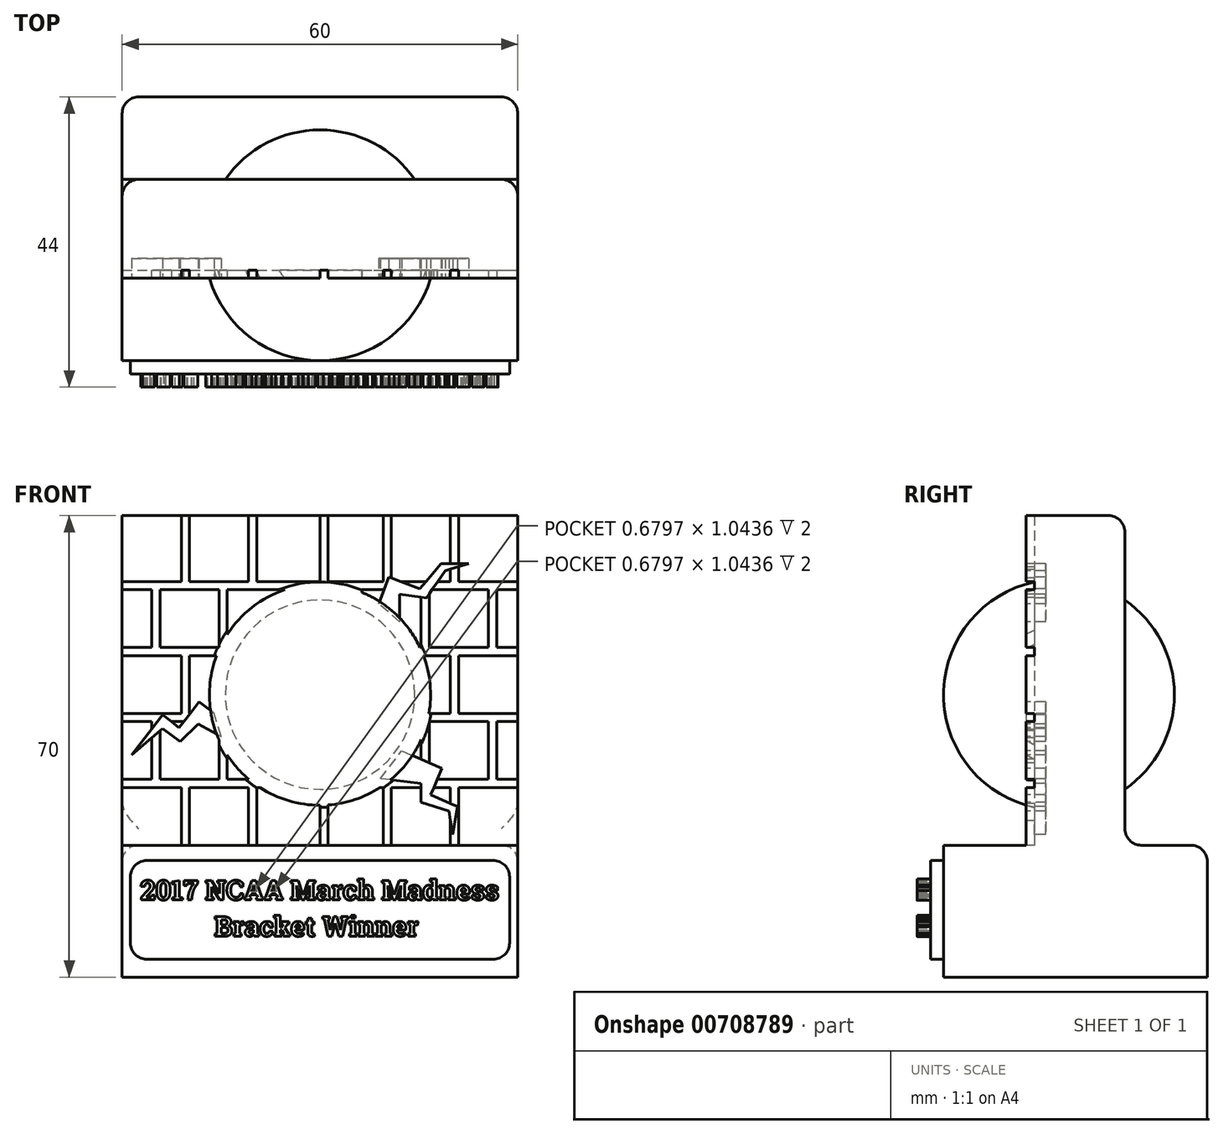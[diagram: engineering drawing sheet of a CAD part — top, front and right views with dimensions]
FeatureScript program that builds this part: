
annotation { "Feature Type Name" : "Feature", "Feature Type Description" : "" }
export const myFeature = defineFeature(function(context is Context, id is Id, definition is map)
    precondition{}
    {
        {
            var Q0;
            Q0=qCreatedBy(makeId("Top.planeOp"),FACE);
            var sketch = newSketch(context, id + "F0", { "sketchPlane" : qUnion([Q0])});
            skLineSegment(sketch, "E0.bottom", {"start": v(30, -20) * mm, "end": v(-30, -20) * mm});
            skLineSegment(sketch, "E0.top", {"start": v(30, 20) * mm, "end": v(-30, 20) * mm});
            skLineSegment(sketch, "E0.left", {"start": v(30, -20) * mm, "end": v(30, 20) * mm});
            skLineSegment(sketch, "E0.right", {"start": v(-30, -20) * mm, "end": v(-30, 20) * mm});
            skPoint(sketch, "E0.middle", {"position": v(0, 0) * mm});
            skSolve(sketch);
        }
        {
            var Q0;
            Q0=makeQuery(id+"F0.imprint","IMPRINT",FACE,{"disambiguationData":[TD([[makeQuery(id+"F0.imprint","IMPRINT",EDGE,{"derivedFrom":sQuery(id+"F0.wireOp",EDGE,"E0.bottom")}),-1.0]])]});
            extrude(context, id + "F1", {"entities" : qUnion([Q0]), "depth" : 20 * mm, "offsetDistance" : 25 * mm});
        }
        {
            var Q0;
            Q0=makeQuery(id+"F1.opExtrude","CAP_FACE",FACE,{"disambiguationData":[OSD([sQuery(id+"F0.wireOp",EDGE,"E0.bottom"),sQuery(id+"F0.wireOp",EDGE,"E0.top"),sQuery(id+"F0.wireOp",EDGE,"E0.left"),sQuery(id+"F0.wireOp",EDGE,"E0.right")])],"isStart":false});
            var sketch = newSketch(context, id + "F2", { "sketchPlane" : qUnion([Q0])});
            skLineSegment(sketch, "E1.bottom", {"start": v(30, -7.5) * mm, "end": v(-30, -7.5) * mm});
            skLineSegment(sketch, "E1.top", {"start": v(30, 7.5) * mm, "end": v(-30, 7.5) * mm});
            skLineSegment(sketch, "E1.left", {"start": v(30, -7.5) * mm, "end": v(30, 7.5) * mm});
            skLineSegment(sketch, "E1.right", {"start": v(-30, -7.5) * mm, "end": v(-30, 7.5) * mm});
            skPoint(sketch, "E1.middle", {"position": v(0, 0) * mm});
            skSolve(sketch);
        }
        {
            var Q0;
            Q0 = qSketchRegion(id + "F2", true);
            extrude(context, id + "F3", {"entities" : qUnion([Q0]), "operationType" : NewBodyOperationType.ADD, "depth" : 50 * mm, "offsetDistance" : 25 * mm});
        }
        {
            var Q0;
            Q0=makeQuery(id+"F3.opExtrude","SWEPT_FACE",FACE,{"disambiguationData":[OSD([sQuery(id+"F2.wireOp",EDGE,"E1.bottom")])]});
            var sketch = newSketch(context, id + "F4", { "sketchPlane" : qUnion([Q0])});
            skSolve(sketch);
        }
        {
            var Q0;
            {var subQ0=sQuery(id+"F2.wireOp",EDGE,"E1.bottom");Q0=makeQuery(id+"F4.imprint","IMPRINT",FACE,{"disambiguationData":[TD([[makeQuery(id+"F4.imprint","IMPRINT",EDGE,{"derivedFrom":makeQuery(id+"F3.opExtrude","CAP_EDGE",EDGE,{"disambiguationData":[OSD([subQ0])],"isStart":false})}),1.0]])]});}
            var sketch = newSketch(context, id + "F5", { "sketchPlane" : qUnion([Q0])});
            skLineSegment(sketch, "E2", {"start": v(-30, 60) * mm, "end": v(-21.04, 60) * mm});
            skLineSegment(sketch, "E3", {"start": v(-30, 50) * mm, "end": v(-25.52, 50) * mm});
            skLineSegment(sketch, "E4", {"start": v(-30, 40) * mm, "end": v(-21.04, 40) * mm});
            skLineSegment(sketch, "E5", {"start": v(-30, 30) * mm, "end": v(-25.52, 30) * mm});
            skLineSegment(sketch, "E6", {"start": v(-30, 58.75) * mm, "end": v(-25.52, 58.75) * mm});
            skLineSegment(sketch, "E7", {"start": v(-30, 48.75) * mm, "end": v(-21.04, 48.75) * mm});
            skLineSegment(sketch, "E8", {"start": v(-30, 38.75) * mm, "end": v(-25.52, 38.75) * mm});
            skLineSegment(sketch, "E9", {"start": v(-30, 28.75) * mm, "end": v(-21.04, 28.75) * mm});
            skLineSegment(sketch, "E10", {"start": v(-30, 60) * mm, "end": v(-30, 58.75) * mm});
            skLineSegment(sketch, "E11", {"start": v(30, 60) * mm, "end": v(30, 58.75) * mm});
            skLineSegment(sketch, "E12.bottom", {"start": v(-21.04, 70) * mm, "end": v(-19.79, 70) * mm});
            skLineSegment(sketch, "E12.left", {"start": v(-21.04, 70) * mm, "end": v(-21.04, 60) * mm});
            skLineSegment(sketch, "E12.right", {"start": v(-19.79, 70) * mm, "end": v(-19.79, 60) * mm});
            skLineSegment(sketch, "E13.bottom", {"start": v(-10.83, 70) * mm, "end": v(-9.58, 70) * mm});
            skLineSegment(sketch, "E13.left", {"start": v(-10.83, 70) * mm, "end": v(-10.83, 60) * mm});
            skLineSegment(sketch, "E13.right", {"start": v(-9.58, 70) * mm, "end": v(-9.58, 60) * mm});
            skLineSegment(sketch, "E14.bottom", {"start": v(9.58, 70) * mm, "end": v(10.83, 70) * mm});
            skLineSegment(sketch, "E14.left", {"start": v(9.58, 70) * mm, "end": v(9.58, 60) * mm});
            skLineSegment(sketch, "E14.right", {"start": v(10.83, 70) * mm, "end": v(10.83, 60) * mm});
            skLineSegment(sketch, "E15.bottom", {"start": v(19.79, 70) * mm, "end": v(21.04, 70) * mm});
            skLineSegment(sketch, "E15.left", {"start": v(19.79, 70) * mm, "end": v(19.79, 60) * mm});
            skLineSegment(sketch, "E15.right", {"start": v(21.04, 70) * mm, "end": v(21.04, 60) * mm});
            skLineSegment(sketch, "E16.top", {"start": v(1.24, 70) * mm, "end": v(-0.01, 70) * mm});
            skLineSegment(sketch, "E16.left", {"start": v(1.24, 60) * mm, "end": v(1.24, 70) * mm});
            skLineSegment(sketch, "E16.right", {"start": v(-0.01, 60) * mm, "end": v(-0.01, 70) * mm});
            skPoint(sketch, "E16.middle", {"position": v(0.61, 65) * mm});
            skLineSegment(sketch, "E17.0", {"start": v(-21.04, 20) * mm, "end": v(-19.79, 20) * mm});
            skLineSegment(sketch, "E18.trimOffspring", {"start": v(-21.04, 48.75) * mm, "end": v(-21.04, 40) * mm});
            skLineSegment(sketch, "E19.trimOffspring", {"start": v(-19.79, 48.75) * mm, "end": v(-19.79, 40) * mm});
            skLineSegment(sketch, "E20.trimOffspring", {"start": v(-10.83, 48.75) * mm, "end": v(-10.83, 40) * mm});
            skLineSegment(sketch, "E21.trimOffspring", {"start": v(-9.58, 48.75) * mm, "end": v(-9.58, 40) * mm});
            skLineSegment(sketch, "E22.trimOffspring", {"start": v(-0.01, 48.75) * mm, "end": v(-0.01, 40) * mm});
            skLineSegment(sketch, "E23.trimOffspring", {"start": v(1.24, 48.75) * mm, "end": v(1.24, 40) * mm});
            skLineSegment(sketch, "E24.trimOffspring", {"start": v(9.58, 48.75) * mm, "end": v(9.58, 40) * mm});
            skLineSegment(sketch, "E25.trimOffspring", {"start": v(10.83, 48.75) * mm, "end": v(10.83, 40) * mm});
            skLineSegment(sketch, "E26.trimOffspring", {"start": v(19.79, 48.75) * mm, "end": v(19.79, 40) * mm});
            skLineSegment(sketch, "E27.trimOffspring", {"start": v(21.04, 48.75) * mm, "end": v(21.04, 40) * mm});
            skLineSegment(sketch, "E28.trimOffspring", {"start": v(-21.04, 28.75) * mm, "end": v(-21.04, 20) * mm});
            skLineSegment(sketch, "E29.trimOffspring", {"start": v(-19.79, 28.75) * mm, "end": v(-19.79, 20) * mm});
            skLineSegment(sketch, "E30.trimOffspring", {"start": v(-10.83, 28.75) * mm, "end": v(-10.83, 20) * mm});
            skLineSegment(sketch, "E31.trimOffspring", {"start": v(-9.58, 28.75) * mm, "end": v(-9.58, 20) * mm});
            skLineSegment(sketch, "E32.trimOffspring", {"start": v(-0.01, 28.75) * mm, "end": v(-0.01, 20) * mm});
            skLineSegment(sketch, "E33.trimOffspring", {"start": v(9.58, 28.75) * mm, "end": v(9.58, 20) * mm});
            skLineSegment(sketch, "E34.trimOffspring", {"start": v(10.83, 28.75) * mm, "end": v(10.83, 20) * mm});
            skLineSegment(sketch, "E35.trimOffspring", {"start": v(19.79, 28.75) * mm, "end": v(19.79, 20) * mm});
            skLineSegment(sketch, "E36.trimOffspring", {"start": v(21.04, 28.75) * mm, "end": v(21.04, 20) * mm});
            skLineSegment(sketch, "E37.trimOffspring", {"start": v(-9.58, 60) * mm, "end": v(9.58, 60) * mm});
            skLineSegment(sketch, "E38.trimOffspring", {"start": v(-19.79, 60) * mm, "end": v(-10.83, 60) * mm});
            skLineSegment(sketch, "E39.trimOffspring", {"start": v(10.83, 48.75) * mm, "end": v(19.79, 48.75) * mm});
            skPoint(sketch, "E40.firstSnap0", {"position": v(-25.52, 60) * mm});
            skLineSegment(sketch, "E40.left", {"start": v(-25.52, 58.75) * mm, "end": v(-25.52, 50) * mm});
            skLineSegment(sketch, "E40.right", {"start": v(-24.27, 58.75) * mm, "end": v(-24.27, 50) * mm});
            skLineSegment(sketch, "E41.left", {"start": v(-15.3, 58.75) * mm, "end": v(-15.3, 50) * mm});
            skLineSegment(sketch, "E41.right", {"start": v(-14.06, 58.75) * mm, "end": v(-14.06, 50) * mm});
            skLineSegment(sketch, "E42.left", {"start": v(-5.1, 58.75) * mm, "end": v(-5.1, 50) * mm});
            skLineSegment(sketch, "E42.right", {"start": v(-3.85, 58.75) * mm, "end": v(-3.85, 50) * mm});
            skLineSegment(sketch, "E43.left", {"start": v(5.11, 58.75) * mm, "end": v(5.11, 50) * mm});
            skLineSegment(sketch, "E43.right", {"start": v(6.36, 58.75) * mm, "end": v(6.36, 50) * mm});
            skLineSegment(sketch, "E44.left", {"start": v(15.32, 58.75) * mm, "end": v(15.32, 50) * mm});
            skLineSegment(sketch, "E44.right", {"start": v(16.57, 58.75) * mm, "end": v(16.57, 50) * mm});
            skLineSegment(sketch, "E45.left", {"start": v(25.53, 58.75) * mm, "end": v(25.53, 50) * mm});
            skLineSegment(sketch, "E45.right", {"start": v(26.78, 58.75) * mm, "end": v(26.78, 50) * mm});
            skLineSegment(sketch, "E46.trimOffspring", {"start": v(-25.52, 38.75) * mm, "end": v(-25.52, 30) * mm});
            skLineSegment(sketch, "E47.trimOffspring", {"start": v(-24.27, 38.75) * mm, "end": v(-24.27, 30) * mm});
            skLineSegment(sketch, "E48.trimOffspring", {"start": v(-15.3, 38.75) * mm, "end": v(-15.3, 30) * mm});
            skLineSegment(sketch, "E49.trimOffspring", {"start": v(-14.06, 38.75) * mm, "end": v(-14.06, 30) * mm});
            skLineSegment(sketch, "E50.trimOffspring", {"start": v(-5.1, 38.75) * mm, "end": v(-5.1, 30) * mm});
            skLineSegment(sketch, "E51.trimOffspring", {"start": v(-3.85, 38.75) * mm, "end": v(-3.85, 30) * mm});
            skLineSegment(sketch, "E52.trimOffspring", {"start": v(5.11, 38.75) * mm, "end": v(5.11, 30) * mm});
            skLineSegment(sketch, "E53.trimOffspring", {"start": v(6.36, 38.75) * mm, "end": v(6.36, 30) * mm});
            skLineSegment(sketch, "E54.trimOffspring", {"start": v(15.32, 38.75) * mm, "end": v(15.32, 30) * mm});
            skLineSegment(sketch, "E55.trimOffspring", {"start": v(16.57, 38.75) * mm, "end": v(16.57, 30) * mm});
            skLineSegment(sketch, "E56.trimOffspring", {"start": v(25.53, 38.75) * mm, "end": v(25.53, 30) * mm});
            skLineSegment(sketch, "E57.trimOffspring", {"start": v(26.78, 38.75) * mm, "end": v(26.78, 30) * mm});
            skPoint(sketch, "E58.orphan", {"position": v(-3.85, 20) * mm});
            skLineSegment(sketch, "E59.trimOffspring", {"start": v(1.24, 28.75) * mm, "end": v(1.24, 20) * mm});
            skLineSegment(sketch, "E60.trimOffspring", {"start": v(-24.27, 58.75) * mm, "end": v(-15.3, 58.75) * mm});
            skLineSegment(sketch, "E61.trimOffspring", {"start": v(-14.06, 58.75) * mm, "end": v(-5.1, 58.75) * mm});
            skLineSegment(sketch, "E62.trimOffspring", {"start": v(-19.79, 48.75) * mm, "end": v(-10.83, 48.75) * mm});
            skLineSegment(sketch, "E63.trimOffspring", {"start": v(-24.27, 50) * mm, "end": v(-15.3, 50) * mm});
            skLineSegment(sketch, "E64.trimOffspring", {"start": v(-9.58, 48.75) * mm, "end": v(-0.01, 48.75) * mm});
            skLineSegment(sketch, "E65.trimOffspring", {"start": v(-3.85, 50) * mm, "end": v(5.11, 50) * mm});
            skLineSegment(sketch, "E66.trimOffspring", {"start": v(-14.06, 50) * mm, "end": v(-5.1, 50) * mm});
            skLineSegment(sketch, "E67.trimOffspring", {"start": v(-3.85, 58.75) * mm, "end": v(5.11, 58.75) * mm});
            skLineSegment(sketch, "E68.trimOffspring", {"start": v(6.36, 58.75) * mm, "end": v(15.32, 58.75) * mm});
            skLineSegment(sketch, "E69.trimOffspring", {"start": v(10.83, 60) * mm, "end": v(19.79, 60) * mm});
            skLineSegment(sketch, "E70.trimOffspring", {"start": v(16.57, 58.75) * mm, "end": v(25.53, 58.75) * mm});
            skLineSegment(sketch, "E71.trimOffspring", {"start": v(21.04, 60) * mm, "end": v(30, 60) * mm});
            skLineSegment(sketch, "E72.trimOffspring", {"start": v(26.78, 58.75) * mm, "end": v(30, 58.75) * mm});
            skLineSegment(sketch, "E73.trimOffspring", {"start": v(19.8, 70) * mm, "end": v(21.04, 70) * mm});
            skLineSegment(sketch, "E74.trimOffspring", {"start": v(-0.01, 70) * mm, "end": v(1.24, 70) * mm});
            skLineSegment(sketch, "E75.trimOffspring", {"start": v(-0.01, 70) * mm, "end": v(10.83, 70) * mm});
            skLineSegment(sketch, "E76.trimOffspring", {"start": v(-30, 50) * mm, "end": v(-30, 48.75) * mm});
            skLineSegment(sketch, "E77.trimOffspring", {"start": v(-30, 40) * mm, "end": v(-30, 38.75) * mm});
            skLineSegment(sketch, "E78.trimOffspring", {"start": v(-30, 30) * mm, "end": v(-30, 28.75) * mm});
            skLineSegment(sketch, "E79.trimOffspring", {"start": v(-10.83, 20) * mm, "end": v(-9.58, 20) * mm});
            skLineSegment(sketch, "E80.trimOffspring", {"start": v(-0.01, 20) * mm, "end": v(1.24, 20) * mm});
            skLineSegment(sketch, "E81.trimOffspring", {"start": v(9.58, 20) * mm, "end": v(10.83, 20) * mm});
            skLineSegment(sketch, "E82.trimOffspring", {"start": v(19.79, 20) * mm, "end": v(21.04, 20) * mm});
            skLineSegment(sketch, "E83.trimOffspring", {"start": v(30, 30) * mm, "end": v(30, 28.75) * mm});
            skLineSegment(sketch, "E84.trimOffspring", {"start": v(30, 40) * mm, "end": v(30, 38.75) * mm});
            skLineSegment(sketch, "E85.trimOffspring", {"start": v(30, 50) * mm, "end": v(30, 48.75) * mm});
            skLineSegment(sketch, "E86.trimOffspring", {"start": v(-19.79, 40) * mm, "end": v(-10.83, 40) * mm});
            skLineSegment(sketch, "E87.trimOffspring", {"start": v(-24.27, 38.75) * mm, "end": v(-15.3, 38.75) * mm});
            skLineSegment(sketch, "E88.trimOffspring", {"start": v(-9.58, 40) * mm, "end": v(-0.01, 40) * mm});
            skLineSegment(sketch, "E89.trimOffspring", {"start": v(-14.06, 38.75) * mm, "end": v(-5.1, 38.75) * mm});
            skLineSegment(sketch, "E90.trimOffspring", {"start": v(-3.85, 38.75) * mm, "end": v(5.11, 38.75) * mm});
            skLineSegment(sketch, "E91.trimOffspring", {"start": v(1.24, 40) * mm, "end": v(9.58, 40) * mm});
            skLineSegment(sketch, "E92.trimOffspring", {"start": v(6.36, 38.75) * mm, "end": v(15.32, 38.75) * mm});
            skLineSegment(sketch, "E93.trimOffspring", {"start": v(10.83, 40) * mm, "end": v(19.79, 40) * mm});
            skLineSegment(sketch, "E94.trimOffspring", {"start": v(16.57, 38.75) * mm, "end": v(25.53, 38.75) * mm});
            skLineSegment(sketch, "E95.trimOffspring", {"start": v(6.36, 50) * mm, "end": v(15.32, 50) * mm});
            skLineSegment(sketch, "E96.trimOffspring", {"start": v(16.57, 50) * mm, "end": v(25.53, 50) * mm});
            skLineSegment(sketch, "E97.trimOffspring", {"start": v(26.78, 50) * mm, "end": v(30, 50) * mm});
            skLineSegment(sketch, "E98.trimOffspring", {"start": v(21.04, 48.75) * mm, "end": v(30, 48.75) * mm});
            skLineSegment(sketch, "E99.trimOffspring", {"start": v(1.24, 48.75) * mm, "end": v(9.58, 48.75) * mm});
            skLineSegment(sketch, "E100.trimOffspring", {"start": v(21.04, 40) * mm, "end": v(30, 40) * mm});
            skLineSegment(sketch, "E101.trimOffspring", {"start": v(26.78, 38.75) * mm, "end": v(30, 38.75) * mm});
            skLineSegment(sketch, "E102.trimOffspring", {"start": v(-24.27, 30) * mm, "end": v(-15.3, 30) * mm});
            skLineSegment(sketch, "E103.trimOffspring", {"start": v(-19.79, 28.75) * mm, "end": v(-10.83, 28.75) * mm});
            skLineSegment(sketch, "E104.trimOffspring", {"start": v(-14.06, 30) * mm, "end": v(-5.1, 30) * mm});
            skLineSegment(sketch, "E105.trimOffspring", {"start": v(-9.58, 28.75) * mm, "end": v(-0.01, 28.75) * mm});
            skLineSegment(sketch, "E106.trimOffspring", {"start": v(-3.85, 30) * mm, "end": v(5.11, 30) * mm});
            skLineSegment(sketch, "E107.trimOffspring", {"start": v(1.24, 28.75) * mm, "end": v(9.58, 28.75) * mm});
            skLineSegment(sketch, "E108.trimOffspring", {"start": v(6.36, 30) * mm, "end": v(15.32, 30) * mm});
            skLineSegment(sketch, "E109.trimOffspring", {"start": v(10.83, 28.75) * mm, "end": v(19.79, 28.75) * mm});
            skLineSegment(sketch, "E110.trimOffspring", {"start": v(16.57, 30) * mm, "end": v(25.53, 30) * mm});
            skLineSegment(sketch, "E111.trimOffspring", {"start": v(26.78, 30) * mm, "end": v(30, 30) * mm});
            skLineSegment(sketch, "E112.trimOffspring", {"start": v(21.04, 28.75) * mm, "end": v(30, 28.75) * mm});
            skSolve(sketch);
        }
        {
            var Q0;
            Q0=makeQuery(id+"F5.imprint","IMPRINT",FACE,{"disambiguationData":[TD([[makeQuery(id+"F5.imprint","IMPRINT",EDGE,{"derivedFrom":sQuery(id+"F5.wireOp",EDGE,"E2")}),-1.0]])]});
            var Q1;
            {var subQ0=sQuery(id+"F5.wireOp",EDGE,"E16.left");Q1=makeQuery(id+"F5.imprint","IMPRINT",FACE,{"disambiguationData":[TD([[makeQuery(id+"F5.imprint","IMPRINT",EDGE,{"derivedFrom":subQ0}),1.0]])]});}
            extrude(context, id + "F6", {"entities" : qUnion([Q0, Q1]), "operationType" : NewBodyOperationType.REMOVE, "oppositeDirection" : true, "depth" : 1.25 * mm, "offsetDistance" : 25 * mm});
        }
        {
            var Q0;
            Q0=makeQuery(id+"F1.opExtrude","SWEPT_FACE",FACE,{"disambiguationData":[OSD([sQuery(id+"F0.wireOp",EDGE,"E0.bottom")])]});
            var sketch = newSketch(context, id + "F7", { "sketchPlane" : qUnion([Q0])});
            skLineSegment(sketch, "E113.bottom", {"start": v(26.25, 2.7) * mm, "end": v(-26.25, 2.7) * mm});
            skLineSegment(sketch, "E113.top", {"start": v(26.25, 17.7) * mm, "end": v(-26.25, 17.7) * mm});
            skLineSegment(sketch, "E113.left", {"start": v(28.75, 5.2) * mm, "end": v(28.75, 15.2) * mm});
            skLineSegment(sketch, "E113.right", {"start": v(-28.75, 5.2) * mm, "end": v(-28.75, 15.2) * mm});
            skPoint(sketch, "E113.middle", {"position": v(0, 10.2) * mm});
            skPoint(sketch, "E114.visualSharp", {"position": v(-28.75, 17.7) * mm});
            skArc(sketch, "E114.filletArc", {"start": v(-26.25, 17.7) * mm, "mid": v(-28.02, 16.96) * mm, "end": v(-28.75, 15.2) * mm});
            skPoint(sketch, "E115.visualSharp", {"position": v(-28.75, 2.7) * mm});
            skArc(sketch, "E115.filletArc", {"start": v(-28.75, 5.2) * mm, "mid": v(-28.02, 3.43) * mm, "end": v(-26.25, 2.7) * mm});
            skPoint(sketch, "E116.visualSharp", {"position": v(28.75, 2.7) * mm});
            skArc(sketch, "E116.filletArc", {"start": v(26.25, 2.7) * mm, "mid": v(28.02, 3.43) * mm, "end": v(28.75, 5.2) * mm});
            skPoint(sketch, "E117.visualSharp", {"position": v(28.75, 17.7) * mm});
            skArc(sketch, "E117.filletArc", {"start": v(28.75, 15.2) * mm, "mid": v(28.02, 16.96) * mm, "end": v(26.25, 17.7) * mm});
            skSolve(sketch);
        }
        {
            var Q0;
            Q0 = qSketchRegion(id + "F7", true);
            extrude(context, id + "F8", {"entities" : qUnion([Q0]), "operationType" : NewBodyOperationType.ADD, "depth" : 2 * mm, "offsetDistance" : 25 * mm});
        }
        {
            var Q0;
            Q0=makeQuery(id+"F8.opExtrude","CAP_FACE",FACE,{"disambiguationData":[OSD([sQuery(id+"F7.wireOp",EDGE,"E113.bottom"),sQuery(id+"F7.wireOp",EDGE,"E113.top"),sQuery(id+"F7.wireOp",EDGE,"E113.left"),sQuery(id+"F7.wireOp",EDGE,"E113.right"),sQuery(id+"F7.wireOp",EDGE,"E114.filletArc"),sQuery(id+"F7.wireOp",EDGE,"E115.filletArc"),sQuery(id+"F7.wireOp",EDGE,"E116.filletArc"),sQuery(id+"F7.wireOp",EDGE,"E117.filletArc")])],"isStart":false});
            var sketch = newSketch(context, id + "F9", { "sketchPlane" : qUnion([Q0])});
            skText(sketch, "E118", { "text": "2017 NCAA March Madness \n           Bracket Winner", "fontName": "RobotoSlab-Bold.ttf"});
            const initialGuessF9  = {"E118": [-0.02725, 0.0117, 1, 0, 0.003]};
            skSetInitialGuess(sketch, initialGuessF9);
            skSolve(sketch);
        }
        {
            var Q0;
            Q0 = qSketchRegion(id + "F9", true);
            extrude(context, id + "F10", {"entities" : qUnion([Q0]), "operationType" : NewBodyOperationType.ADD, "depth" : 2 * mm, "offsetDistance" : 25 * mm});
        }
        {
            var Q0;
            Q0=qCreatedBy(makeId("Front.planeOp"),FACE);
            cPlane(context, id + "F11", {"entities" : qUnion([Q0]), "cplaneType" : CPlaneType.OFFSET, "offset" : 2.5 * mm, "width" : 150 * mm, "height" : 150 * mm});
        }
        {
            var Q0;
            Q0=qCreatedBy(id+"F11.planeOp",FACE);
            var sketch = newSketch(context, id + "F12", { "sketchPlane" : qUnion([Q0])});
            skArc(sketch, "E119", {"start": v(0, 25.34) * mm, "mid": v(17.5, 42.84) * mm, "end": v(0, 60.34) * mm});
            skLineSegment(sketch, "E120", {"start": v(0, 60.34) * mm, "end": v(0, 25.34) * mm});
            skLineSegment(sketch, "E121", {"start": v(0, 65.18) * mm, "end": v(0, 22.01) * mm, "construction": true});
            skSolve(sketch);
        }
        {
            var Q0;
            Q0 = qSketchRegion(id + "F12", true);
            var Q1;
            Q1=sQuery(id+"F12.wireOp",EDGE,"E119");
            var Q2;
            Q2=sQuery(id+"F12.wireOp",EDGE,"E121");
            revolve(context, id + "F13", {"operationType" : NewBodyOperationType.ADD, "surfaceOperationType" : NewSurfaceOperationType.NEW, "entities" : qUnion([Q0]), "surfaceEntities" : qUnion([Q1]), "axis" : qUnion([Q2]), "revolveType" : RevolveType.FULL});
        }
        {
            var Q0;
            {var subQ0=sQuery(id+"F2.wireOp",EDGE,"E1.bottom");Q0=makeQuery(id+"F4.imprint","IMPRINT",FACE,{"disambiguationData":[TD([[makeQuery(id+"F4.imprint","IMPRINT",EDGE,{"derivedFrom":makeQuery(id+"F3.opExtrude","CAP_EDGE",EDGE,{"disambiguationData":[OSD([subQ0])],"isStart":false})}),1.0]])]});}
            var sketch = newSketch(context, id + "F14", { "sketchPlane" : qUnion([Q0])});
            skLineSegment(sketch, "E122", {"start": v(8.92, 56.64) * mm, "end": v(10.44, 60.68) * mm});
            skLineSegment(sketch, "E123", {"start": v(10.44, 60.68) * mm, "end": v(15.12, 58.92) * mm});
            skLineSegment(sketch, "E124", {"start": v(15.12, 58.92) * mm, "end": v(18.39, 62.7) * mm});
            skLineSegment(sketch, "E125", {"start": v(18.39, 62.7) * mm, "end": v(22.55, 62.7) * mm});
            skLineSegment(sketch, "E126", {"start": v(-16.05, 40) * mm, "end": v(-18.32, 41.76) * mm});
            skLineSegment(sketch, "E127", {"start": v(-18.32, 41.76) * mm, "end": v(-21.37, 37.84) * mm});
            skLineSegment(sketch, "E128", {"start": v(-21.37, 37.84) * mm, "end": v(-23.85, 39.77) * mm});
            skLineSegment(sketch, "E129", {"start": v(-23.85, 39.77) * mm, "end": v(-28.58, 33.69) * mm});
            skLineSegment(sketch, "E130", {"start": v(12.42, 34.3) * mm, "end": v(18.51, 31.67) * mm});
            skLineSegment(sketch, "E131", {"start": v(18.51, 31.67) * mm, "end": v(16.77, 27.64) * mm});
            skLineSegment(sketch, "E132", {"start": v(16.77, 27.64) * mm, "end": v(20.86, 25.87) * mm});
            skLineSegment(sketch, "E133", {"start": v(20.86, 25.87) * mm, "end": v(20.17, 21.64) * mm});
            skLineSegment(sketch, "E134", {"start": v(20.17, 21.64) * mm, "end": v(19.54, 25.17) * mm});
            skLineSegment(sketch, "E135", {"start": v(19.54, 25.17) * mm, "end": v(15.31, 26.5) * mm});
            skLineSegment(sketch, "E136", {"start": v(15.31, 26.5) * mm, "end": v(15.31, 29.4) * mm});
            skLineSegment(sketch, "E137", {"start": v(15.31, 29.4) * mm, "end": v(9.15, 30.1) * mm});
            skLineSegment(sketch, "E138", {"start": v(9.15, 30.1) * mm, "end": v(12.42, 34.3) * mm});
            skLineSegment(sketch, "E139", {"start": v(22.55, 62.7) * mm, "end": v(18.97, 61.65) * mm});
            skLineSegment(sketch, "E140", {"start": v(18.97, 61.65) * mm, "end": v(16.15, 57.52) * mm});
            skLineSegment(sketch, "E141", {"start": v(16.15, 57.52) * mm, "end": v(12.07, 58.05) * mm});
            skLineSegment(sketch, "E142", {"start": v(12.07, 58.05) * mm, "end": v(12.07, 53.88) * mm});
            skLineSegment(sketch, "E143", {"start": v(12.07, 53.88) * mm, "end": v(8.92, 56.64) * mm});
            skLineSegment(sketch, "E144", {"start": v(-28.58, 33.69) * mm, "end": v(-23.85, 37.7) * mm});
            skLineSegment(sketch, "E145", {"start": v(-23.85, 37.7) * mm, "end": v(-21.22, 35.7) * mm});
            skLineSegment(sketch, "E146", {"start": v(-21.22, 35.7) * mm, "end": v(-18.45, 38.38) * mm});
            skLineSegment(sketch, "E147", {"start": v(-18.45, 38.38) * mm, "end": v(-14.97, 36.5) * mm});
            skLineSegment(sketch, "E148", {"start": v(-14.97, 36.5) * mm, "end": v(-16.05, 40) * mm});
            skSolve(sketch);
        }
        {
            var Q0;
            Q0 = qSketchRegion(id + "F14", true);
            extrude(context, id + "F15", {"entities" : qUnion([Q0]), "operationType" : NewBodyOperationType.REMOVE, "oppositeDirection" : true, "depth" : 3 * mm, "offsetDistance" : 25 * mm});
        }
        {
            var Q0;
            {var subQ0=sQuery(id+"F0.wireOp",EDGE,"E0.left");var subQ1=sQuery(id+"F0.wireOp",EDGE,"E0.right");var subQ2=sQuery(id+"F0.wireOp",EDGE,"E0.top");Q0=makeQuery(id+"F3.boolean.opBoolean","SPLIT",FACE,{"disambiguationData":[TD([makeQuery(id+"F1.opExtrude","SWEPT_FACE",FACE,{"disambiguationData":[OSD([subQ2])]})])],"derivedFrom":makeQuery(id+"F1.opExtrude","CAP_FACE",FACE,{"disambiguationData":[OSD([sQuery(id+"F0.wireOp",EDGE,"E0.bottom"),subQ2,subQ0,subQ1])],"isStart":false})});}
            var Q1;
            Q1=makeQuery(id+"F3.opExtrude","CAP_EDGE",EDGE,{"disambiguationData":[OSD([sQuery(id+"F2.wireOp",EDGE,"E1.top")])],"isStart":false});
            var Q2;
            Q2=makeQuery(id+"F1.opExtrude","SWEPT_EDGE",EDGE,{"disambiguationData":[OSD([sQuery(id+"F0.wireOp",EDGE,"E0.top"),sQuery(id+"F0.wireOp",EDGE,"E0.right")])]});
            var Q3;
            Q3=makeQuery(id+"F1.opExtrude","SWEPT_EDGE",EDGE,{"disambiguationData":[OSD([sQuery(id+"F0.wireOp",EDGE,"E0.top"),sQuery(id+"F0.wireOp",EDGE,"E0.left")])]});
            fillet(context, id + "F16", {"entities" : qUnion([Q0, Q1, Q2, Q3]), "radius" : 2.5 * mm, "tangentPropagation" : true, "allowEdgeOverflow" : false});
        }
    });
